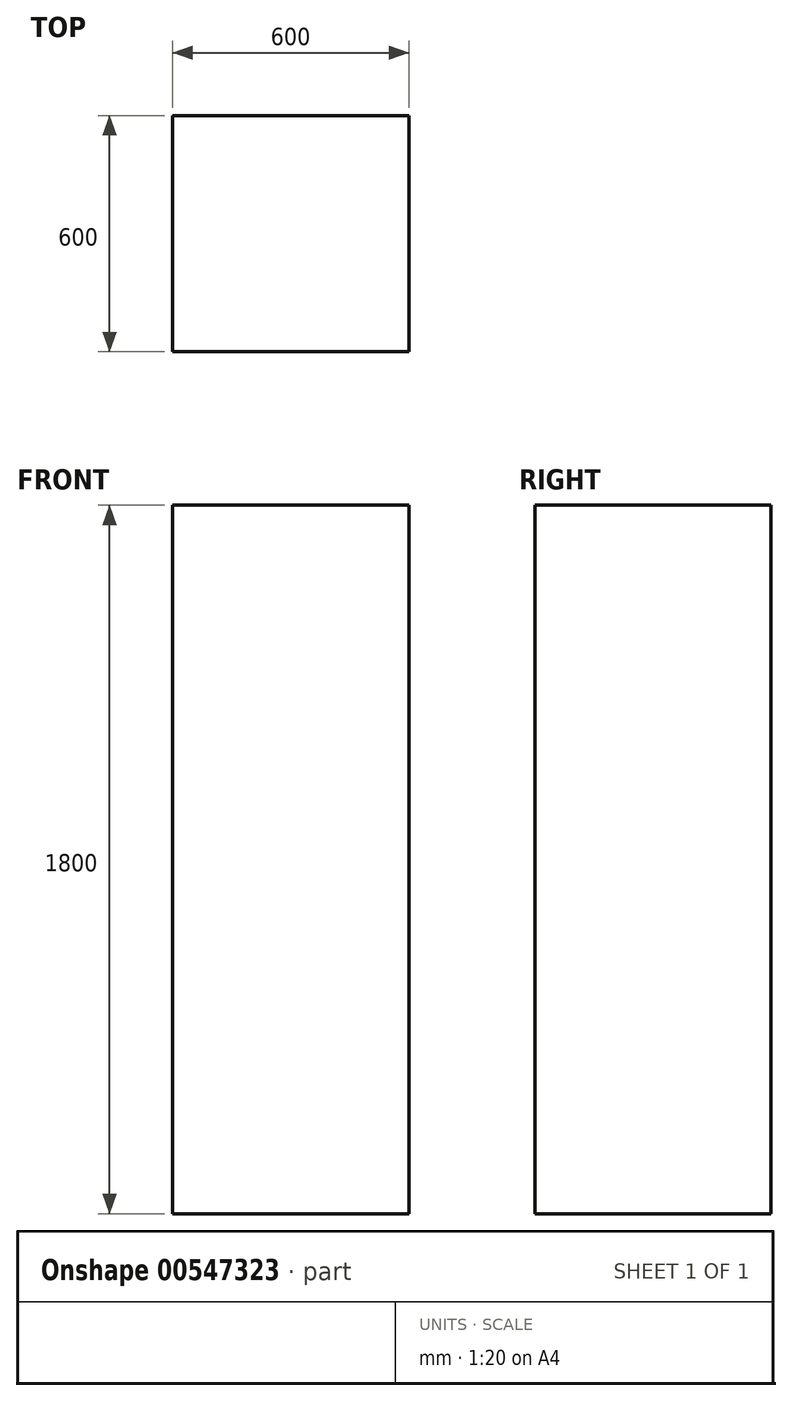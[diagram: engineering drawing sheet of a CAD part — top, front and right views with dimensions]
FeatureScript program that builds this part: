
annotation { "Feature Type Name" : "Feature", "Feature Type Description" : "" }
export const myFeature = defineFeature(function(context is Context, id is Id, definition is map)
    precondition{}
    {
        {
            var Q0;
            Q0=qCreatedBy(makeId("Top.planeOp"),FACE);
            var sketch = newSketch(context, id + "F0", { "sketchPlane" : qUnion([Q0])});
            skLineSegment(sketch, "E0.bottom", {"start": v(300, -300) * mm, "end": v(-300, -300) * mm});
            skLineSegment(sketch, "E0.top", {"start": v(300, 300) * mm, "end": v(-300, 300) * mm});
            skLineSegment(sketch, "E0.left", {"start": v(300, -300) * mm, "end": v(300, 300) * mm});
            skLineSegment(sketch, "E0.right", {"start": v(-300, -300) * mm, "end": v(-300, 300) * mm});
            skPoint(sketch, "E0.middle", {"position": v(0, 0) * mm});
            skSolve(sketch);
        }
        {
            var Q0;
            Q0=makeQuery(id+"F0.imprint","IMPRINT",FACE,{"disambiguationData":[TD([[makeQuery(id+"F0.imprint","IMPRINT",EDGE,{"derivedFrom":sQuery(id+"F0.wireOp",EDGE,"E0.bottom")}),-1.0]])]});
            extrude(context, id + "F1", {"entities" : qUnion([Q0]), "depth" : 1800 * mm, "offsetDistance" : 25 * mm});
        }
    });
